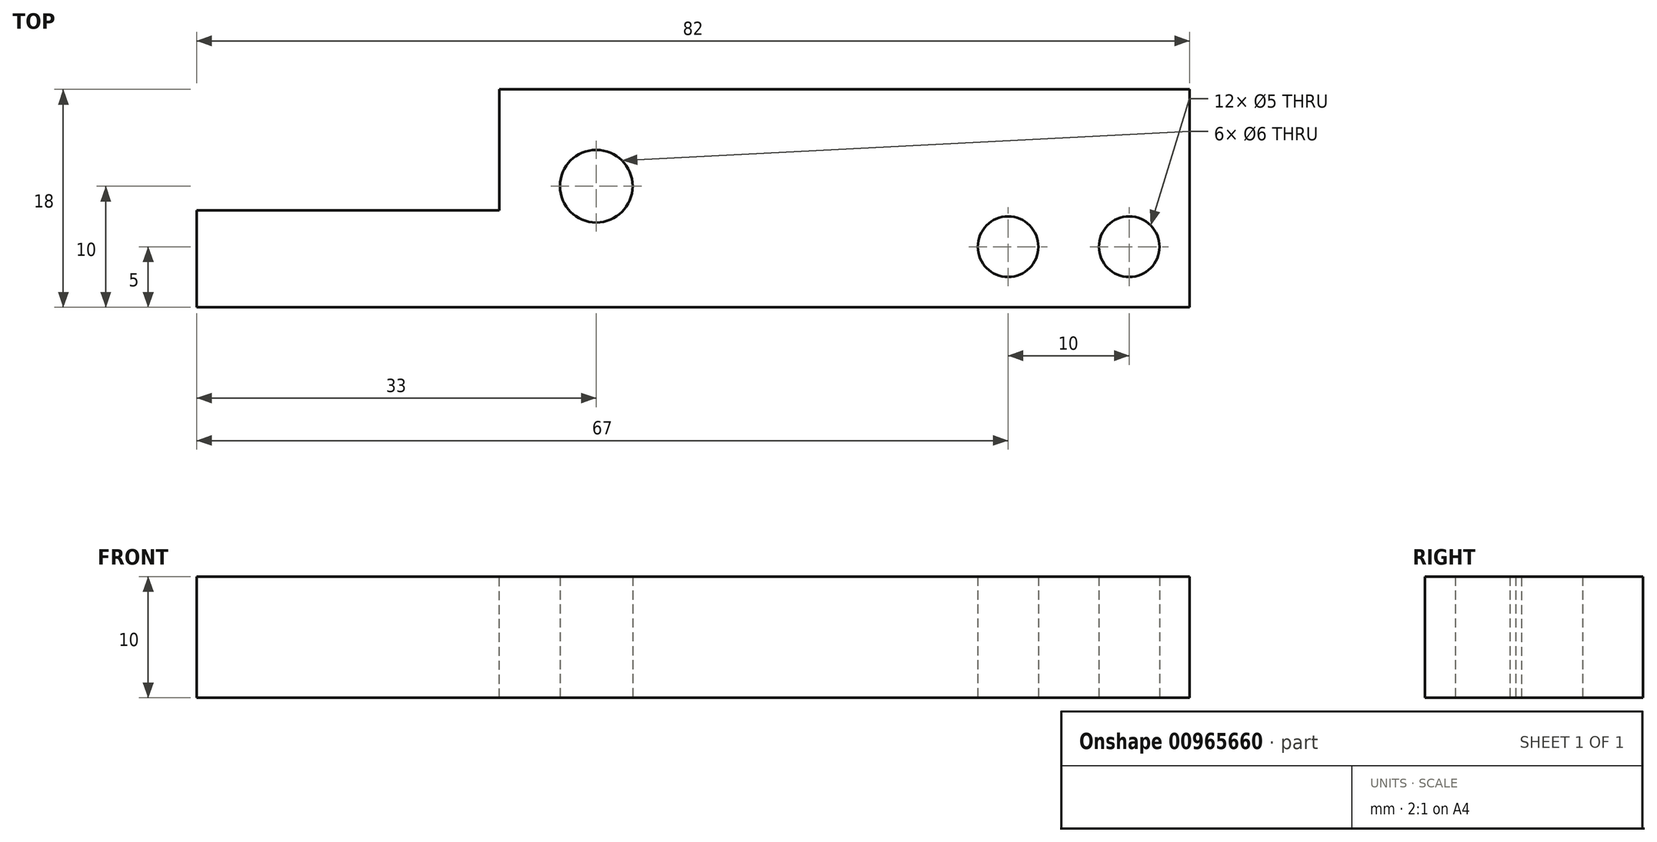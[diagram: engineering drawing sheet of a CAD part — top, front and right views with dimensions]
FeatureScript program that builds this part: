
annotation { "Feature Type Name" : "Feature", "Feature Type Description" : "" }
export const myFeature = defineFeature(function(context is Context, id is Id, definition is map)
    precondition{}
    {
        {
            var Q0;
            Q0=qCreatedBy(makeId("Top.planeOp"),FACE);
            var sketch = newSketch(context, id + "F0", { "sketchPlane" : qUnion([Q0])});
            skLineSegment(sketch, "E0.bottom", {"start": v(41, -10) * mm, "end": v(-41, -10) * mm});
            skLineSegment(sketch, "E0.top", {"start": v(41, 10) * mm, "end": v(-41, 10) * mm});
            skLineSegment(sketch, "E0.left", {"start": v(41, -10) * mm, "end": v(41, 10) * mm});
            skLineSegment(sketch, "E0.right", {"start": v(-41, -10) * mm, "end": v(-41, 10) * mm});
            skPoint(sketch, "E0.middle", {"position": v(0, 0) * mm});
            skCircle(sketch, "E1", {"center": v(36, -5) * mm, "radius": 2.5 * mm});
            skCircle(sketch, "E2", {"center": v(26, -5) * mm, "radius": 2.5 * mm});
            skCircle(sketch, "E3", {"center": v(-8, 0) * mm, "radius": 3 * mm});
            skSolve(sketch);
        }
        {
            var Q0;
            Q0=makeQuery(id+"F0.imprint","IMPRINT",FACE,{"disambiguationData":[TD([[makeQuery(id+"F0.imprint","IMPRINT",EDGE,{"derivedFrom":sQuery(id+"F0.wireOp",EDGE,"E0.bottom")}),-1.0]])]});
            extrude(context, id + "F1", {"entities" : qUnion([Q0]), "depth" : 10 * mm, "offsetDistance" : 25 * mm});
        }
        {
            var Q0;
            Q0=makeQuery(id+"F1.opExtrude","CAP_FACE",FACE,{"disambiguationData":[OSD([sQuery(id+"F0.wireOp",EDGE,"E0.bottom"),sQuery(id+"F0.wireOp",EDGE,"E0.top"),sQuery(id+"F0.wireOp",EDGE,"E0.left"),sQuery(id+"F0.wireOp",EDGE,"E0.right"),sQuery(id+"F0.wireOp",EDGE,"E1"),sQuery(id+"F0.wireOp",EDGE,"E2"),sQuery(id+"F0.wireOp",EDGE,"E3")])],"isStart":false});
            var sketch = newSketch(context, id + "F2", { "sketchPlane" : qUnion([Q0])});
            skLineSegment(sketch, "E4.bottom", {"start": v(-41, 10) * mm, "end": v(-16, 10) * mm});
            skLineSegment(sketch, "E4.top", {"start": v(-41, -2) * mm, "end": v(-16, -2) * mm});
            skLineSegment(sketch, "E4.left", {"start": v(-41, 10) * mm, "end": v(-41, -2) * mm});
            skLineSegment(sketch, "E4.right", {"start": v(-16, 10) * mm, "end": v(-16, -2) * mm});
            skLineSegment(sketch, "E5.bottom", {"start": v(-16, 10) * mm, "end": v(41, 10) * mm});
            skLineSegment(sketch, "E5.top", {"start": v(-16, 8) * mm, "end": v(41, 8) * mm});
            skLineSegment(sketch, "E5.left", {"start": v(-16, 10) * mm, "end": v(-16, 8) * mm});
            skLineSegment(sketch, "E5.right", {"start": v(41, 10) * mm, "end": v(41, 8) * mm});
            skSolve(sketch);
        }
        {
            var Q0;
            Q0=makeQuery(id+"F2.imprint","IMPRINT",FACE,{"disambiguationData":[TD([[makeQuery(id+"F2.imprint","IMPRINT",EDGE,{"derivedFrom":sQuery(id+"F2.wireOp",EDGE,"E4.bottom")}),1.0]])]});
            var Q1;
            Q1=makeQuery(id+"F2.imprint","IMPRINT",FACE,{"disambiguationData":[TD([[makeQuery(id+"F2.imprint","IMPRINT",EDGE,{"derivedFrom":sQuery(id+"F2.wireOp",EDGE,"Duz13YFy-XlIE-9PGH-lg7W-MJikAohBXR9k.bottom")}),-1.0]])]});
            var Q2;
            Q2=makeQuery(id+"F2.imprint","IMPRINT",FACE,{"disambiguationData":[TD([[makeQuery(id+"F2.imprint","IMPRINT",EDGE,{"derivedFrom":sQuery(id+"F2.wireOp",EDGE,"E5.bottom")}),1.0]])]});
            extrude(context, id + "F3", {"entities" : qUnion([Q0, Q1, Q2]), "operationType" : NewBodyOperationType.REMOVE, "oppositeDirection" : true, "depth" : 10 * mm, "offsetDistance" : 25 * mm});
        }
    });
